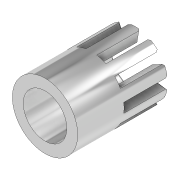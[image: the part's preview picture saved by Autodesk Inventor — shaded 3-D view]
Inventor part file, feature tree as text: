
AUTODESK INVENTOR PART (.ipt)
format: ipt  version: 2020 (Build 240168000, 168)  size: 208,384 bytes
history: native  units: in
note: dims shown in document units (in); Inventor stores cm internally (conversion verified against a paired STEP export)
features: extrude x2, sketch x2, chamfer x1, projected_geometry x1
ambient origin geometry x8: Origin, YZ Plane, XZ Plane, XY Plane, X Axis, Y Axis, Z Axis, Center Point
bodies: Solid1 (feature_tree)
feature tree (6):
  extrude  "Extrusion1"  Depth=0.315in
  extrude  "Extrusion2"  Depth=0.0787in
  chamfer  "Chamfer1"  Distance=0.0394in
  sketch  "Sketch1"  dims[d0=0.4724in d1=0.315in]
  sketch  "Sketch2"  dims[d2=0.3346in d3=0.0in d4=0.0787in d5=0.0394in d6=3.937in d8=360.0deg d10=0.315in d11=0.0in d12=0.0118in d13=0.125in d14=45.0deg]
  projected_geometry  "Projected Loop1"
